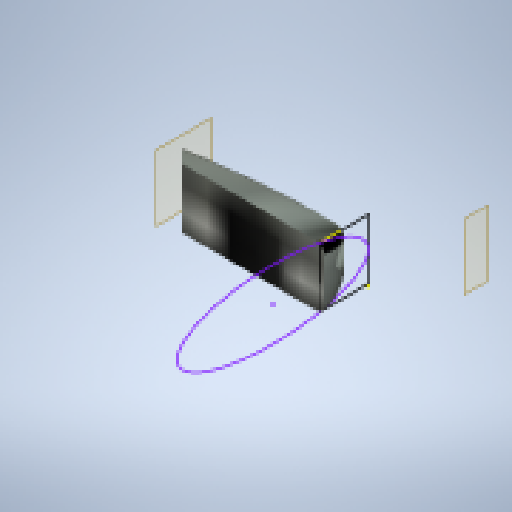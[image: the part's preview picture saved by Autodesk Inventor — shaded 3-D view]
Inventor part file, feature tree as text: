
AUTODESK INVENTOR PART (.ipt)
format: ipt  version: 2025.2 (Build 292293000, 293)  size: 321,536 bytes
history: native  units: in
note: dims shown in document units (in); Inventor stores cm internally (conversion verified against a paired STEP export)
features: reference x18, other x7, extrude x5, sketch x4, fillet x2, projected_geometry x2
ambient origin geometry x8: Origin, YZ Plane, XZ Plane, XY Plane, X Axis, Y Axis, Z Axis, Center Point
bodies: Body1 (feature_tree), Body2 (feature_tree), Body3 (feature_tree), Body4 (feature_tree)
feature tree (38):
  other  "ソリッド1"
  extrude  "押し出し1"  Depth=0.7874in TaperAngle=0.0deg
  extrude  "押し出し2"  TaperAngle=0.0deg  [1 undecoded]
  other  "作業平面3"
  sketch  "スケッチ5"
  extrude  "押し出し3"  Depth=3.937in TaperAngle=0.0deg
  extrude  "押し出し4"  Depth=3.937in TaperAngle=0.0deg
  extrude  "押し出し5"  Depth=3.937in TaperAngle=0.0deg
  fillet  "フィレット1"  Radius=0.1575in
  fillet  "フィレット2"  Radius=0.1181in
  other  "作業平面4"
  sketch  "スケッチ1"
  reference  "参照1"
  reference  "参照3"
  reference  "参照4"
  reference  "参照5"
  reference  "参照6"
  reference  "参照7"
  reference  "参照8"
  reference  "参照9"
  reference  "参照10"
  reference  "参照11"
  reference  "参照12"
  reference  "参照13"
  reference  "参照14"
  reference  "参照15"
  sketch  "スケッチ2"
  reference  "参照16"
  reference  "参照17"
  reference  "参照18"
  reference  "参照19"
  sketch  "スケッチ6"
  projected_geometry  "投影ループ1"
  projected_geometry  "投影ループ2"
  other  "<userpath>\OneDrive\ドキュメント\New Controller\Hardware\Assembly.iam"
  other  "Assembly.iam"
  other  "Body_compleat01:1"
  other  "Body_compleat02:1"
note: 1 required parameter value undecoded (feature->parameter linkage not recoverable at this tier; creation-order binding heuristic only, values carry confidence <= 0.55)
